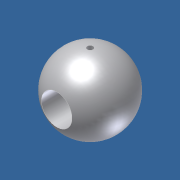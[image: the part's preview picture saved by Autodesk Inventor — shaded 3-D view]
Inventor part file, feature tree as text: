
AUTODESK INVENTOR PART (.ipt)
format: ipt  version: unknown  size: 202,240 bytes
history: native  units: in
note: dims shown in document units (in); Inventor stores cm internally (conversion verified against a paired STEP export)
features: sketch x3, plane x2, hole x2, revolve x1
ambient origin geometry x8: Origin, YZ Plane, XZ Plane, XY Plane, X Axis, Y Axis, Z Axis, Center Point
bodies: Solid1 (feature_tree)
feature tree (8):
  revolve  "Revolution1"  Angle=90.0deg
  plane  "Work Plane1"
  hole  "Hole1"  [1 undecoded]
  plane  "Work Plane2"
  hole  "Hole2"  [1 undecoded]
  sketch  "Sketch1"  dims[d0=0.75in d1=90.0deg]
  sketch  "Sketch2"  dims[d2=0.3125in d3=0.75in d4=0.375in d5=0.25in d6=0.5635in d7=1.0in d8=0.0in]
  sketch  "Sketch3"  dims[d9=0.06in d10=0.75in d11=0.375in d12=0.25in d13=0.5635in d14=1.0in d15=0.0in]
note: 2 required parameter values undecoded (feature->parameter linkage not recoverable at this tier; creation-order binding heuristic only, values carry confidence <= 0.55)
